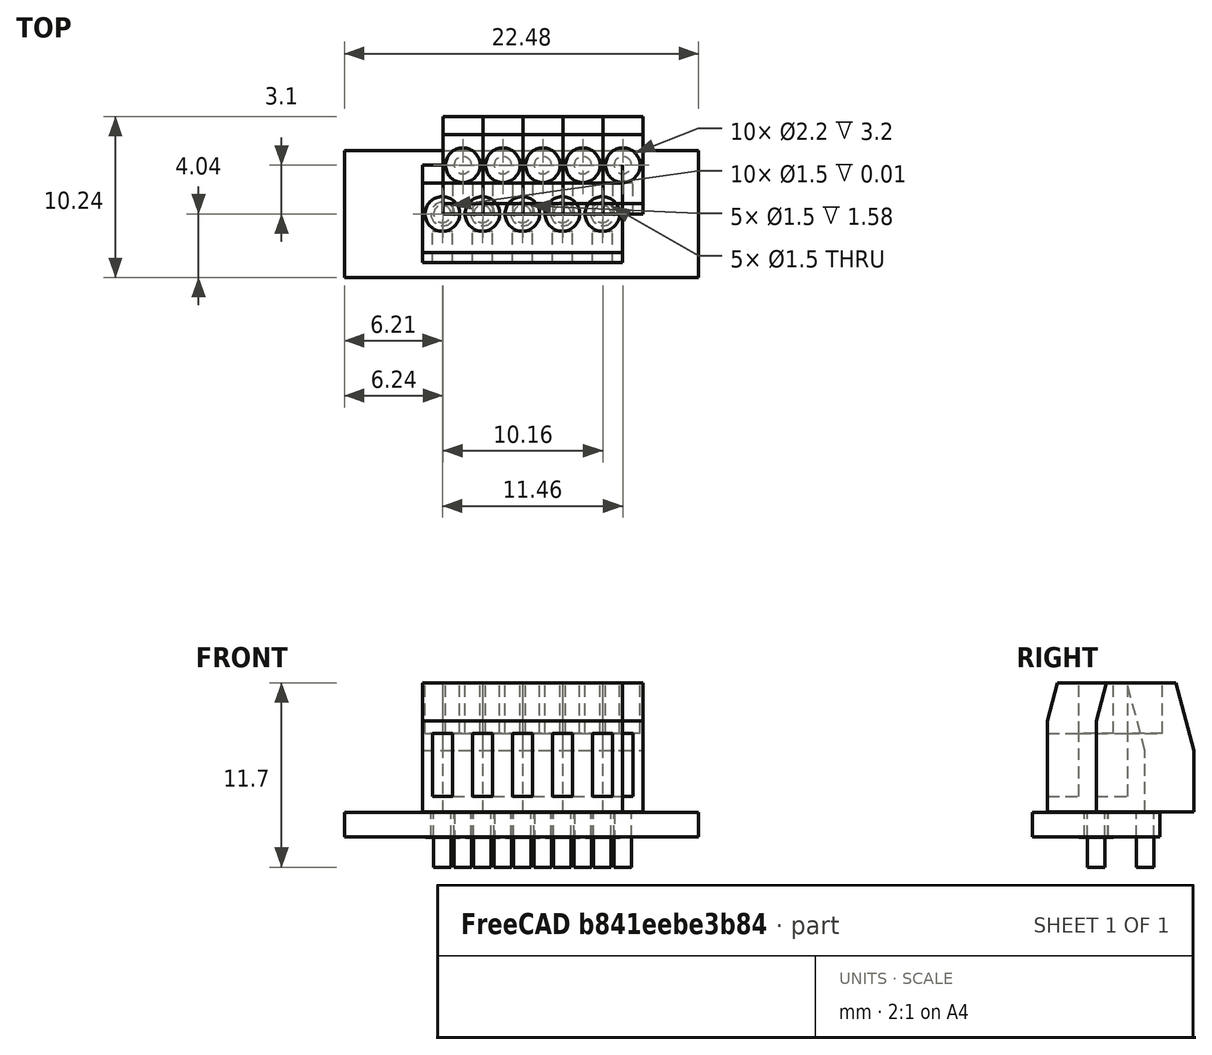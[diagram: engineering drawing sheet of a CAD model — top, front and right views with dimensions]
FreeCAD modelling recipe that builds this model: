
FCSTD DOCUMENT  (FreeCAD 0.19R18353 (Git))
Label: screw_terminal
License: All rights reserved
LicenseURL: http://en.wikipedia.org/wiki/All_rights_reserved
objects: Part::Box×20, Part::Cut×20, Part::Cylinder×10, Part::FeaturePython×7, Part::Fuse×5, App::DocumentObjectGroup×1, Part::Feature×1
note: 63 computed .brp shape members not serialized (recipe doc carries the construction recipe); baked Part::Feature solids carry a one-line shape summary decoded from their .brp

FEATURE [Part::Box] cube
  AttacherType = Attacher::AttachEngine3D
  Height = 8.2
  Length = 2.54
  Width = 6.2
FEATURE [Part::Box] cube001
  AttacherType = Attacher::AttachEngine3D
  Height = 4
  Length = 1.27
  Placement = pos=(0.635,-1,1) rot=(0,0,1;0rad)
  Width = 3
FEATURE [Part::Cut] difference
  Base = -> cube
  Tool = -> cube001
FEATURE [Part::Box] cube002
  AttacherType = Attacher::AttachEngine3D
  Height = 8
  Length = 4
  Placement = pos=(-1,6.76148,1.81173) rot=(1,0,0;0.261799rad)
  Width = 6
FEATURE [Part::Cut] difference001
  Base = -> difference
  Tool = -> cube002
FEATURE [Part::Box] cube003
  AttacherType = Attacher::AttachEngine3D
  Height = 9
  Length = 4
  Placement = pos=(-1,-7.24444,1.94114) rot=(-1,0,0;0.261799rad)
  Width = 6
FEATURE [Part::Cut] difference002
  Base = -> difference001
  Tool = -> cube003
FEATURE [Part::Cylinder] cylinder
  Angle = 360
  AttacherType = Attacher::AttachEngine3D
  Height = 3.5
  Placement = pos=(1.27,3.1,5) rot=(0,0,1;0rad)
  Radius = 1.1
FEATURE [Part::Cut] difference003
  Base = -> difference002
  Tool = -> cylinder
FEATURE [Part::Cylinder] cylinder001
  Angle = 360
  AttacherType = Attacher::AttachEngine3D
  Height = 3.5
  Placement = pos=(1.27,3.1,-3.5) rot=(0,0,1;0rad)
  Radius = 0.55
FEATURE [Part::Fuse] Group
  Base = -> difference003
  Tool = -> cylinder001
FEATURE [Part::Box] cube004
  AttacherType = Attacher::AttachEngine3D
  Height = 8.2
  Length = 2.54
  Width = 6.2
FEATURE [Part::Box] cube005
  AttacherType = Attacher::AttachEngine3D
  Height = 4
  Length = 1.27
  Placement = pos=(0.635,-1,1) rot=(0,0,1;0rad)
  Width = 3
FEATURE [Part::Cut] difference004
  Base = -> cube004
  Tool = -> cube005
FEATURE [Part::Box] cube006
  AttacherType = Attacher::AttachEngine3D
  Height = 8
  Length = 4
  Placement = pos=(-1,6.76148,1.81173) rot=(1,0,0;0.261799rad)
  Width = 6
FEATURE [Part::Cut] difference005
  Base = -> difference004
  Tool = -> cube006
FEATURE [Part::Box] cube007
  AttacherType = Attacher::AttachEngine3D
  Height = 9
  Length = 4
  Placement = pos=(-1,-7.24444,1.94114) rot=(-1,0,0;0.261799rad)
  Width = 6
FEATURE [Part::Cut] difference006
  Base = -> difference005
  Tool = -> cube007
FEATURE [Part::Cylinder] cylinder002
  Angle = 360
  AttacherType = Attacher::AttachEngine3D
  Height = 3.5
  Placement = pos=(1.27,3.1,5) rot=(0,0,1;0rad)
  Radius = 1.1
FEATURE [Part::Cut] difference007
  Base = -> difference006
  Tool = -> cylinder002
FEATURE [Part::Cylinder] cylinder003
  Angle = 360
  AttacherType = Attacher::AttachEngine3D
  Height = 3.5
  Placement = pos=(1.27,3.1,-3.5) rot=(0,0,1;0rad)
  Radius = 0.55
FEATURE [Part::Fuse] Group001
  Base = -> difference007
  Placement = pos=(2.54,0,0) rot=(0,0,1;0rad)
  Tool = -> cylinder003
FEATURE [Part::Box] cube008
  AttacherType = Attacher::AttachEngine3D
  Height = 8.2
  Length = 2.54
  Width = 6.2
FEATURE [Part::Box] cube009
  AttacherType = Attacher::AttachEngine3D
  Height = 4
  Length = 1.27
  Placement = pos=(0.635,-1,1) rot=(0,0,1;0rad)
  Width = 3
FEATURE [Part::Cut] difference008
  Base = -> cube008
  Tool = -> cube009
FEATURE [Part::Box] cube010
  AttacherType = Attacher::AttachEngine3D
  Height = 8
  Length = 4
  Placement = pos=(-1,6.76148,1.81173) rot=(1,0,0;0.261799rad)
  Width = 6
FEATURE [Part::Cut] difference009
  Base = -> difference008
  Tool = -> cube010
FEATURE [Part::Box] cube011
  AttacherType = Attacher::AttachEngine3D
  Height = 9
  Length = 4
  Placement = pos=(-1,-7.24444,1.94114) rot=(-1,0,0;0.261799rad)
  Width = 6
FEATURE [Part::Cut] difference010
  Base = -> difference009
  Tool = -> cube011
FEATURE [Part::Cylinder] cylinder004
  Angle = 360
  AttacherType = Attacher::AttachEngine3D
  Height = 3.5
  Placement = pos=(1.27,3.1,5) rot=(0,0,1;0rad)
  Radius = 1.1
FEATURE [Part::Cut] difference011
  Base = -> difference010
  Tool = -> cylinder004
FEATURE [Part::Cylinder] cylinder005
  Angle = 360
  AttacherType = Attacher::AttachEngine3D
  Height = 3.5
  Placement = pos=(1.27,3.1,-3.5) rot=(0,0,1;0rad)
  Radius = 0.55
FEATURE [Part::Fuse] Group002
  Base = -> difference011
  Placement = pos=(5.08,0,0) rot=(0,0,1;0rad)
  Tool = -> cylinder005
FEATURE [Part::Box] cube012
  AttacherType = Attacher::AttachEngine3D
  Height = 8.2
  Length = 2.54
  Width = 6.2
FEATURE [Part::Box] cube013
  AttacherType = Attacher::AttachEngine3D
  Height = 4
  Length = 1.27
  Placement = pos=(0.635,-1,1) rot=(0,0,1;0rad)
  Width = 3
FEATURE [Part::Cut] difference012
  Base = -> cube012
  Tool = -> cube013
FEATURE [Part::Box] cube014
  AttacherType = Attacher::AttachEngine3D
  Height = 8
  Length = 4
  Placement = pos=(-1,6.76148,1.81173) rot=(1,0,0;0.261799rad)
  Width = 6
FEATURE [Part::Cut] difference013
  Base = -> difference012
  Tool = -> cube014
FEATURE [Part::Box] cube015
  AttacherType = Attacher::AttachEngine3D
  Height = 9
  Length = 4
  Placement = pos=(-1,-7.24444,1.94114) rot=(-1,0,0;0.261799rad)
  Width = 6
FEATURE [Part::Cut] difference014
  Base = -> difference013
  Tool = -> cube015
FEATURE [Part::Cylinder] cylinder006
  Angle = 360
  AttacherType = Attacher::AttachEngine3D
  Height = 3.5
  Placement = pos=(1.27,3.1,5) rot=(0,0,1;0rad)
  Radius = 1.1
FEATURE [Part::Cut] difference015
  Base = -> difference014
  Tool = -> cylinder006
FEATURE [Part::Cylinder] cylinder007
  Angle = 360
  AttacherType = Attacher::AttachEngine3D
  Height = 3.5
  Placement = pos=(1.27,3.1,-3.5) rot=(0,0,1;0rad)
  Radius = 0.55
FEATURE [Part::Fuse] Group003
  Base = -> difference015
  Placement = pos=(7.62,0,0) rot=(0,0,1;0rad)
  Tool = -> cylinder007
FEATURE [Part::Box] cube016
  AttacherType = Attacher::AttachEngine3D
  Height = 8.2
  Length = 2.54
  Width = 6.2
FEATURE [Part::Box] cube017
  AttacherType = Attacher::AttachEngine3D
  Height = 4
  Length = 1.27
  Placement = pos=(0.635,-1,1) rot=(0,0,1;0rad)
  Width = 3
FEATURE [Part::Cut] difference016
  Base = -> cube016
  Tool = -> cube017
FEATURE [Part::Box] cube018
  AttacherType = Attacher::AttachEngine3D
  Height = 8
  Length = 4
  Placement = pos=(-1,6.76148,1.81173) rot=(1,0,0;0.261799rad)
  Width = 6
FEATURE [Part::Cut] difference017
  Base = -> difference016
  Tool = -> cube018
FEATURE [Part::Box] cube019
  AttacherType = Attacher::AttachEngine3D
  Height = 9
  Length = 4
  Placement = pos=(-1,-7.24444,1.94114) rot=(-1,0,0;0.261799rad)
  Width = 6
FEATURE [Part::Cut] difference018
  Base = -> difference017
  Tool = -> cube019
FEATURE [Part::Cylinder] cylinder008
  Angle = 360
  AttacherType = Attacher::AttachEngine3D
  Height = 3.5
  Placement = pos=(1.27,3.1,5) rot=(0,0,1;0rad)
  Radius = 1.1
FEATURE [Part::Cut] difference019
  Base = -> difference018
  Tool = -> cylinder008
FEATURE [Part::Cylinder] cylinder009
  Angle = 360
  AttacherType = Attacher::AttachEngine3D
  Height = 3.5
  Placement = pos=(1.27,3.1,-3.5) rot=(0,0,1;0rad)
  Radius = 0.55
FEATURE [Part::Fuse] Group004
  Base = -> difference019
  Placement = pos=(10.16,0,0) rot=(0,0,1;0rad)
  Tool = -> cylinder009
FEATURE [Part::FeaturePython] FCrtYd_lines  label="FCrtYd"  # a2plus imported part (geometry in sourceFile) (typed FeaturePython)
  fixedPosition = true
FEATURE [Part::FeaturePython] FFab_lines  label="FFab"  # a2plus imported part (geometry in sourceFile) (typed FeaturePython)
  fixedPosition = true
FEATURE [Part::FeaturePython] Filk_lines  label="FrontSilk"  # a2plus imported part (geometry in sourceFile) (typed FeaturePython)
  fixedPosition = true
FEATURE [Part::FeaturePython] TopPads  # a2plus imported part (geometry in sourceFile) (typed FeaturePython)
  fixedPosition = true
FEATURE [Part::FeaturePython] BotPads  # a2plus imported part (geometry in sourceFile) (typed FeaturePython)
  fixedPosition = true
FEATURE [Part::FeaturePython] THPs  label="PTHs"  # a2plus imported part (geometry in sourceFile) (typed FeaturePython)
  fixedPosition = true
FEATURE [Part::FeaturePython] newPCB  label="Pcb"  # a2plus imported part (geometry in sourceFile) (typed FeaturePython)
  fixedPosition = true
FEATURE [App::DocumentObjectGroup] TerminalBlock_1x05_Horizontal_ScrewM2_54_fp
  Group = -> [FCrtYd_lines,FFab_lines,Filk_lines,TopPads,BotPads,THPs,newPCB]
FEATURE [Part::Feature] Shape  label="Group005"
  shape: bbox 12.7 x 6.2 x 11.7 mm, 77 faces (baked)
